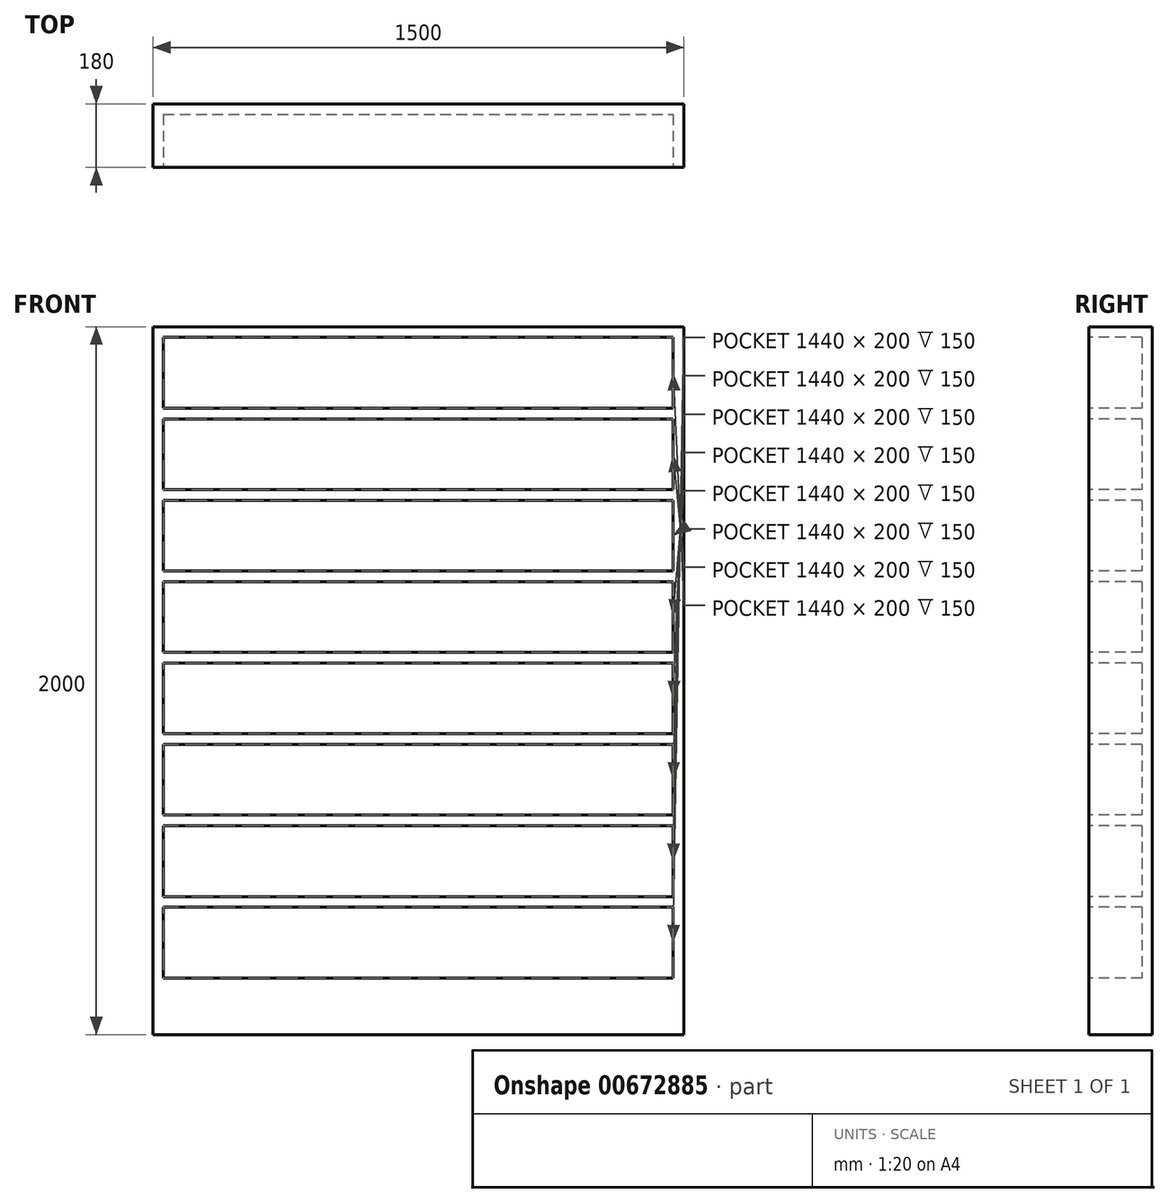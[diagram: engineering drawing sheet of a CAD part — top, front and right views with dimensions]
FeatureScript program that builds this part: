
annotation { "Feature Type Name" : "Feature", "Feature Type Description" : "" }
export const myFeature = defineFeature(function(context is Context, id is Id, definition is map)
    precondition{}
    {
        {
            var Q0;
            Q0=qCreatedBy(makeId("Front.planeOp"),FACE);
            var sketch = newSketch(context, id + "F0", { "sketchPlane" : qUnion([Q0])});
            skLineSegment(sketch, "E0.bottom", {"start": v(0, 0) * mm, "end": v(1500, 0) * mm});
            skLineSegment(sketch, "E0.top", {"start": v(0, 2000) * mm, "end": v(1500, 2000) * mm});
            skLineSegment(sketch, "E0.left", {"start": v(0, 0) * mm, "end": v(0, 2000) * mm});
            skLineSegment(sketch, "E0.right", {"start": v(1500, 0) * mm, "end": v(1500, 2000) * mm});
            skSolve(sketch);
        }
        {
            var Q0;
            Q0 = qSketchRegion(id + "F0", true);
            extrude(context, id + "F1", {"entities" : qUnion([Q0]), "depth" : 180 * mm, "offsetDistance" : 25 * mm});
        }
        {
            var Q0;
            Q0=makeQuery(id+"F1.opExtrude","CAP_FACE",FACE,{"disambiguationData":[OSD([sQuery(id+"F0.wireOp",EDGE,"E0.bottom"),sQuery(id+"F0.wireOp",EDGE,"E0.top"),sQuery(id+"F0.wireOp",EDGE,"E0.left"),sQuery(id+"F0.wireOp",EDGE,"E0.right")])],"isStart":false});
            var sketch = newSketch(context, id + "F2", { "sketchPlane" : qUnion([Q0])});
            skLineSegment(sketch, "E1.bottom", {"start": v(30, 1970) * mm, "end": v(1470, 1970) * mm});
            skLineSegment(sketch, "E1.top", {"start": v(30, 1770) * mm, "end": v(1470, 1770) * mm});
            skLineSegment(sketch, "E1.left", {"start": v(30, 1970) * mm, "end": v(30, 1770) * mm});
            skLineSegment(sketch, "E1.right", {"start": v(1470, 1970) * mm, "end": v(1470, 1770) * mm});
            skLineSegment(sketch, "E2.0.1.0", {"start": v(30, 1740) * mm, "end": v(1470, 1740) * mm});
            skLineSegment(sketch, "E2.0.1.1", {"start": v(30, 1740) * mm, "end": v(30, 1540) * mm});
            skLineSegment(sketch, "E2.0.1.2", {"start": v(30, 1540) * mm, "end": v(1470, 1540) * mm});
            skLineSegment(sketch, "E2.0.1.3", {"start": v(1470, 1740) * mm, "end": v(1470, 1540) * mm});
            skLineSegment(sketch, "E2.0.2.0", {"start": v(30, 1510) * mm, "end": v(1470, 1510) * mm});
            skLineSegment(sketch, "E2.0.2.1", {"start": v(30, 1510) * mm, "end": v(30, 1310) * mm});
            skLineSegment(sketch, "E2.0.2.2", {"start": v(30, 1310) * mm, "end": v(1470, 1310) * mm});
            skLineSegment(sketch, "E2.0.2.3", {"start": v(1470, 1510) * mm, "end": v(1470, 1310) * mm});
            skLineSegment(sketch, "E2.0.3.0", {"start": v(30, 1280) * mm, "end": v(1470, 1280) * mm});
            skLineSegment(sketch, "E2.0.3.1", {"start": v(30, 1280) * mm, "end": v(30, 1080) * mm});
            skLineSegment(sketch, "E2.0.3.2", {"start": v(30, 1080) * mm, "end": v(1470, 1080) * mm});
            skLineSegment(sketch, "E2.0.3.3", {"start": v(1470, 1280) * mm, "end": v(1470, 1080) * mm});
            skLineSegment(sketch, "E2.0.4.0", {"start": v(30, 1050) * mm, "end": v(1470, 1050) * mm});
            skLineSegment(sketch, "E2.0.4.1", {"start": v(30, 1050) * mm, "end": v(30, 850) * mm});
            skLineSegment(sketch, "E2.0.4.2", {"start": v(30, 850) * mm, "end": v(1470, 850) * mm});
            skLineSegment(sketch, "E2.0.4.3", {"start": v(1470, 1050) * mm, "end": v(1470, 850) * mm});
            skLineSegment(sketch, "E2.direction1", {"start": v(30, 1770) * mm, "end": v(55, 1770) * mm, "construction": true});
            skLineSegment(sketch, "E2.direction2", {"start": v(30, 1770) * mm, "end": v(30, 1540) * mm, "construction": true});
            skLineSegment(sketch, "E3.0.0.5", {"start": v(30, 820) * mm, "end": v(1470, 820) * mm});
            skLineSegment(sketch, "E3.3.0.5", {"start": v(30, 820) * mm, "end": v(30, 620) * mm});
            skLineSegment(sketch, "E3.6.0.5", {"start": v(30, 620) * mm, "end": v(1470, 620) * mm});
            skLineSegment(sketch, "E3.9.0.5", {"start": v(1470, 820) * mm, "end": v(1470, 620) * mm});
            skLineSegment(sketch, "E3.0.0.6", {"start": v(30, 590) * mm, "end": v(1470, 590) * mm});
            skLineSegment(sketch, "E3.3.0.6", {"start": v(30, 590) * mm, "end": v(30, 390) * mm});
            skLineSegment(sketch, "E3.6.0.6", {"start": v(30, 390) * mm, "end": v(1470, 390) * mm});
            skLineSegment(sketch, "E3.9.0.6", {"start": v(1470, 590) * mm, "end": v(1470, 390) * mm});
            skLineSegment(sketch, "E3.0.0.7", {"start": v(30, 360) * mm, "end": v(1470, 360) * mm});
            skLineSegment(sketch, "E3.3.0.7", {"start": v(30, 360) * mm, "end": v(30, 160) * mm});
            skLineSegment(sketch, "E3.6.0.7", {"start": v(30, 160) * mm, "end": v(1470, 160) * mm});
            skLineSegment(sketch, "E3.9.0.7", {"start": v(1470, 360) * mm, "end": v(1470, 160) * mm});
            skSolve(sketch);
        }
        {
            var Q0;
            Q0 = qSketchRegion(id + "F2", true);
            extrude(context, id + "F3", {"entities" : qUnion([Q0]), "operationType" : NewBodyOperationType.REMOVE, "oppositeDirection" : true, "depth" : 150 * mm, "offsetDistance" : 25 * mm});
        }
    });
